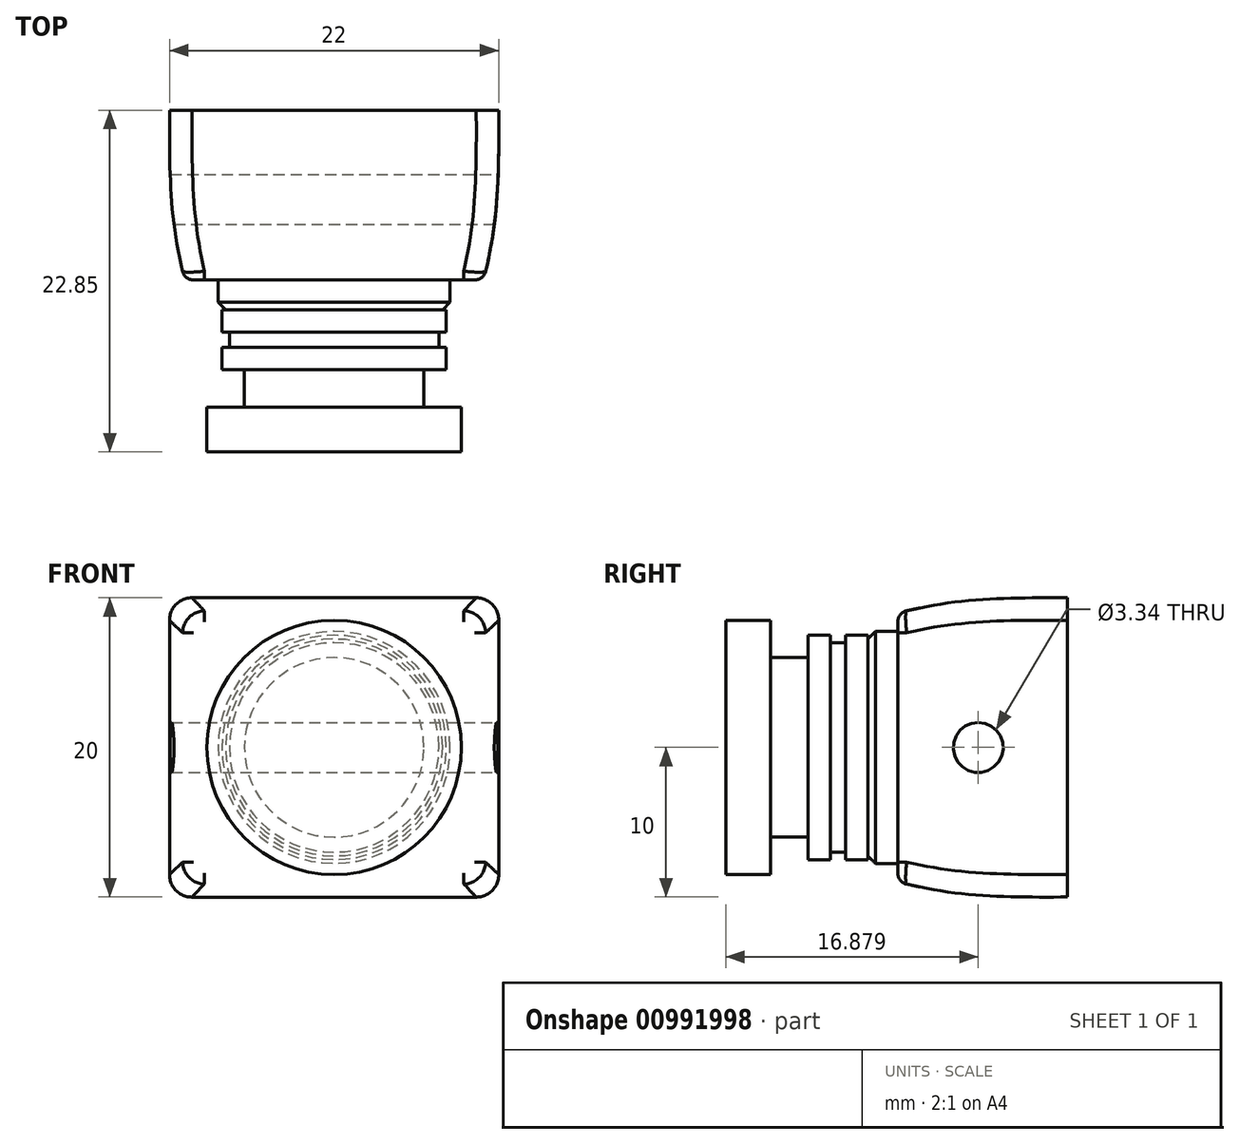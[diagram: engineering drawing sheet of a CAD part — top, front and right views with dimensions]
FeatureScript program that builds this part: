
annotation { "Feature Type Name" : "Feature", "Feature Type Description" : "" }
export const myFeature = defineFeature(function(context is Context, id is Id, definition is map)
    precondition{}
    {
        {
            var Q0;
            Q0=qCreatedBy(makeId("Front.planeOp"),FACE);
            var sketch = newSketch(context, id + "F0", { "sketchPlane" : qUnion([Q0])});
            skLineSegment(sketch, "E0.bottom", {"start": v(11, -10) * mm, "end": v(-11, -10) * mm});
            skLineSegment(sketch, "E0.top", {"start": v(11, 10) * mm, "end": v(-11, 10) * mm});
            skLineSegment(sketch, "E0.left", {"start": v(11, -10) * mm, "end": v(11, 10) * mm});
            skLineSegment(sketch, "E0.right", {"start": v(-11, -10) * mm, "end": v(-11, 10) * mm});
            skPoint(sketch, "E0.middle", {"position": v(0, 0) * mm});
            skSolve(sketch);
        }
        {
            var Q0;
            Q0=qCreatedBy(makeId("Front.planeOp"),FACE);
            cPlane(context, id + "F1", {"entities" : qUnion([Q0]), "cplaneType" : CPlaneType.OFFSET, "offset" : 11.35 * mm, "width" : 150 * mm, "height" : 150 * mm});
        }
        {
            var Q0;
            Q0=qCreatedBy(id+"F1.planeOp",FACE);
            var sketch = newSketch(context, id + "F2", { "sketchPlane" : qUnion([Q0])});
            skLineSegment(sketch, "E1.bottom", {"start": v(10, -9) * mm, "end": v(-10, -9) * mm});
            skLineSegment(sketch, "E1.top", {"start": v(10, 9) * mm, "end": v(-10, 9) * mm});
            skLineSegment(sketch, "E1.left", {"start": v(10, -9) * mm, "end": v(10, 9) * mm});
            skLineSegment(sketch, "E1.right", {"start": v(-10, -9) * mm, "end": v(-10, 9) * mm});
            skPoint(sketch, "E1.middle", {"position": v(0, 0) * mm});
            skSolve(sketch);
        }
        {
            var Q0;
            Q0=qCreatedBy(makeId("Front.planeOp"),FACE);
            cPlane(context, id + "F3", {"entities" : qUnion([Q0]), "cplaneType" : CPlaneType.OFFSET, "offset" : 9 * mm, "width" : 150 * mm, "height" : 150 * mm});
        }
        {
            var Q0;
            Q0=qCreatedBy(id+"F3.planeOp",FACE);
            var sketch = newSketch(context, id + "F4", { "sketchPlane" : qUnion([Q0])});
            skLineSegment(sketch, "E2.bottom", {"start": v(10.5, -9.5) * mm, "end": v(-10.5, -9.5) * mm});
            skLineSegment(sketch, "E2.top", {"start": v(10.5, 9.5) * mm, "end": v(-10.5, 9.5) * mm});
            skLineSegment(sketch, "E2.left", {"start": v(10.5, -9.5) * mm, "end": v(10.5, 9.5) * mm});
            skLineSegment(sketch, "E2.right", {"start": v(-10.5, -9.5) * mm, "end": v(-10.5, 9.5) * mm});
            skPoint(sketch, "E2.middle", {"position": v(0, 0) * mm});
            skSolve(sketch);
        }
        {
            var Q0;
            Q0=qSketchRegion(id+"F0",true);
            var Q1;
            Q1=qSketchRegion(id+"F4",true);
            var Q2;
            Q2=qSketchRegion(id+"F2",true);
            loft(context, id + "F5", {"sheetProfilesArray" : [{ "sheetProfileEntities" : qUnion([Q0]) }, { "sheetProfileEntities" : qUnion([Q1]) }, { "sheetProfileEntities" : qUnion([Q2]) }]});
        }
        {
            var Q0;
            Q0=makeQuery(id+"F5.opLoft","SWEPT_EDGE",EDGE,{"disambiguationData":[OSD([sQuery(id+"F0.wireOp",EDGE,"E0.top"),sQuery(id+"F0.wireOp",EDGE,"E0.left"),sQuery(id+"F2.wireOp",EDGE,"E1.top"),sQuery(id+"F2.wireOp",EDGE,"E1.left"),sQuery(id+"F4.wireOp",EDGE,"E2.top"),sQuery(id+"F4.wireOp",EDGE,"E2.left")])]});
            var Q1;
            Q1=makeQuery(id+"F5.opLoft","SWEPT_EDGE",EDGE,{"disambiguationData":[OSD([sQuery(id+"F0.wireOp",EDGE,"E0.top"),sQuery(id+"F0.wireOp",EDGE,"E0.right"),sQuery(id+"F2.wireOp",EDGE,"E1.top"),sQuery(id+"F2.wireOp",EDGE,"E1.right"),sQuery(id+"F4.wireOp",EDGE,"E2.top"),sQuery(id+"F4.wireOp",EDGE,"E2.right")])]});
            var Q2;
            Q2=makeQuery(id+"F5.opLoft","SWEPT_EDGE",EDGE,{"disambiguationData":[OSD([sQuery(id+"F0.wireOp",EDGE,"E0.bottom"),sQuery(id+"F0.wireOp",EDGE,"E0.right"),sQuery(id+"F2.wireOp",EDGE,"E1.bottom"),sQuery(id+"F2.wireOp",EDGE,"E1.right"),sQuery(id+"F4.wireOp",EDGE,"E2.bottom"),sQuery(id+"F4.wireOp",EDGE,"E2.right")])]});
            var Q3;
            Q3=makeQuery(id+"F5.opLoft","SWEPT_EDGE",EDGE,{"disambiguationData":[OSD([sQuery(id+"F0.wireOp",EDGE,"E0.bottom"),sQuery(id+"F0.wireOp",EDGE,"E0.left"),sQuery(id+"F2.wireOp",EDGE,"E1.bottom"),sQuery(id+"F2.wireOp",EDGE,"E1.left"),sQuery(id+"F4.wireOp",EDGE,"E2.bottom"),sQuery(id+"F4.wireOp",EDGE,"E2.left")])]});
            fillet(context, id + "F6", {"entities" : qUnion([Q0, Q1, Q2, Q3]), "radius" : 1.5 * mm, "tangentPropagation" : true, "allowEdgeOverflow" : false});
        }
        {
            var Q0;
            Q0=makeQuery(id+"F5.opLoft","MID_CAP_EDGE",EDGE,{"disambiguationData":[OSD([sQuery(id+"F2.wireOp",EDGE,"E1.top"),sQuery(id+"F2.wireOp",EDGE,"E1.left"),sQuery(id+"F2.wireOp",EDGE,"E1.right")])],"capPos":2.0});
            fillet(context, id + "F7", {"entities" : qUnion([Q0]), "radius" : 0.75 * mm, "tangentPropagation" : true, "allowEdgeOverflow" : false});
        }
        {
            var Q0;
            Q0=makeQuery(id+"F5.opLoft","CAP_FACE",FACE,{"disambiguationData":[OSD([makeQuery(id+"F2.imprint","IMPRINT",FACE,{"disambiguationData":[TD([[makeQuery(id+"F2.imprint","IMPRINT",EDGE,{"derivedFrom":sQuery(id+"F2.wireOp",EDGE,"E1.bottom")}),-1.0]])]})])],"isStart":true});
            var sketch = newSketch(context, id + "F8", { "sketchPlane" : qUnion([Q0])});
            skCircle(sketch, "E3", {"center": v(0, 0) * mm, "radius": 7.75 * mm});
            skSolve(sketch);
        }
        {
            var Q0;
            Q0=qSketchRegion(id+"F8",true);
            extrude(context, id + "F9", {"entities" : qUnion([Q0]), "operationType" : NewBodyOperationType.ADD, "depth" : 2 * mm, "offsetDistance" : 25 * mm});
        }
        {
            var Q0;
            Q0=makeQuery(id+"F9.opExtrude","CAP_EDGE",EDGE,{"disambiguationData":[OSD([sQuery(id+"F8.wireOp",EDGE,"E3")])],"isStart":false});
            chamfer(context, id + "F10", {"entities" : qUnion([Q0]), "width" : 0.5 * mm, "tangentPropagation" : true});
        }
        {
            var Q0;
            Q0=makeQuery(id+"F9.opExtrude","CAP_FACE",FACE,{"disambiguationData":[OSD([sQuery(id+"F8.wireOp",EDGE,"E3")])],"isStart":false});
            var sketch = newSketch(context, id + "F11", { "sketchPlane" : qUnion([Q0])});
            skCircle(sketch, "E4", {"center": v(0, 0) * mm, "radius": 7.5 * mm});
            skSolve(sketch);
        }
        {
            var Q0;
            Q0=qSketchRegion(id+"F11",true);
            extrude(context, id + "F12", {"entities" : qUnion([Q0]), "depth" : 1.5 * mm, "offsetDistance" : 25 * mm});
        }
        {
            var Q0;
            Q0=makeQuery(id+"F12.opExtrude","CAP_FACE",FACE,{"disambiguationData":[OSD([sQuery(id+"F11.wireOp",EDGE,"E4")])],"isStart":false});
            var sketch = newSketch(context, id + "F13", { "sketchPlane" : qUnion([Q0])});
            skCircle(sketch, "E5", {"center": v(0, 0) * mm, "radius": 7 * mm});
            skSolve(sketch);
        }
        {
            var Q0;
            Q0=qSketchRegion(id+"F13",true);
            extrude(context, id + "F14", {"entities" : qUnion([Q0]), "operationType" : NewBodyOperationType.ADD, "depth" : 1 * mm, "offsetDistance" : 25 * mm});
        }
        {
            var Q0;
            Q0=makeQuery(id+"F14.opExtrude","CAP_FACE",FACE,{"disambiguationData":[OSD([sQuery(id+"F13.wireOp",EDGE,"E5")])],"isStart":false});
            var sketch = newSketch(context, id + "F15", { "sketchPlane" : qUnion([Q0])});
            skCircle(sketch, "E6", {"center": v(0, 0) * mm, "radius": 7.5 * mm});
            skSolve(sketch);
        }
        {
            var Q0;
            Q0=qSketchRegion(id+"F15",true);
            extrude(context, id + "F16", {"entities" : qUnion([Q0]), "operationType" : NewBodyOperationType.ADD, "depth" : 1.5 * mm, "offsetDistance" : 25 * mm});
        }
        {
            var Q0;
            Q0=makeQuery(id+"F16.opExtrude","CAP_FACE",FACE,{"disambiguationData":[OSD([sQuery(id+"F15.wireOp",EDGE,"E6")])],"isStart":false});
            var sketch = newSketch(context, id + "F17", { "sketchPlane" : qUnion([Q0])});
            skCircle(sketch, "E7", {"center": v(0, 0) * mm, "radius": 6 * mm});
            skSolve(sketch);
        }
        {
            var Q0;
            Q0=qSketchRegion(id+"F17",true);
            extrude(context, id + "F18", {"entities" : qUnion([Q0]), "operationType" : NewBodyOperationType.ADD, "depth" : 2.5 * mm, "offsetDistance" : 25 * mm});
        }
        {
            var Q0;
            Q0=makeQuery(id+"F18.opExtrude","CAP_FACE",FACE,{"disambiguationData":[OSD([sQuery(id+"F17.wireOp",EDGE,"E7")])],"isStart":false});
            var sketch = newSketch(context, id + "F19", { "sketchPlane" : qUnion([Q0])});
            skCircle(sketch, "E8", {"center": v(0, 0) * mm, "radius": 8.5 * mm});
            skSolve(sketch);
        }
        {
            var Q0;
            Q0=qSketchRegion(id+"F19",true);
            extrude(context, id + "F20", {"entities" : qUnion([Q0]), "operationType" : NewBodyOperationType.ADD, "depth" : 3 * mm, "offsetDistance" : 25 * mm});
        }
        {
            var Q0;
            Q0=qCreatedBy(makeId("Right.planeOp"),FACE);
            var sketch = newSketch(context, id + "F21", { "sketchPlane" : qUnion([Q0])});
            skCircle(sketch, "E9", {"center": v(-5.97, 0) * mm, "radius": 1.67 * mm});
            skSolve(sketch);
        }
        {
            var Q0;
            Q0=qSketchRegion(id+"F21",true);
            extrude(context, id + "F22", {"entities" : qUnion([Q0]), "operationType" : NewBodyOperationType.ADD, "endBound" : BoundingType.SYMMETRIC, "depth" : 24.4 * mm, "offsetDistance" : 25 * mm});
        }
        {
            var Q0;
            Q0=makeQuery(id+"F22.opExtrude","CAP_FACE",FACE,{"disambiguationData":[OSD([sQuery(id+"F21.wireOp",EDGE,"E9")])],"isStart":false});
            extrude(context, id + "F23", {"entities" : qUnion([Q0]), "operationType" : NewBodyOperationType.REMOVE, "oppositeDirection" : true, "depth" : 25 * mm, "offsetDistance" : 25 * mm});
        }
    });
